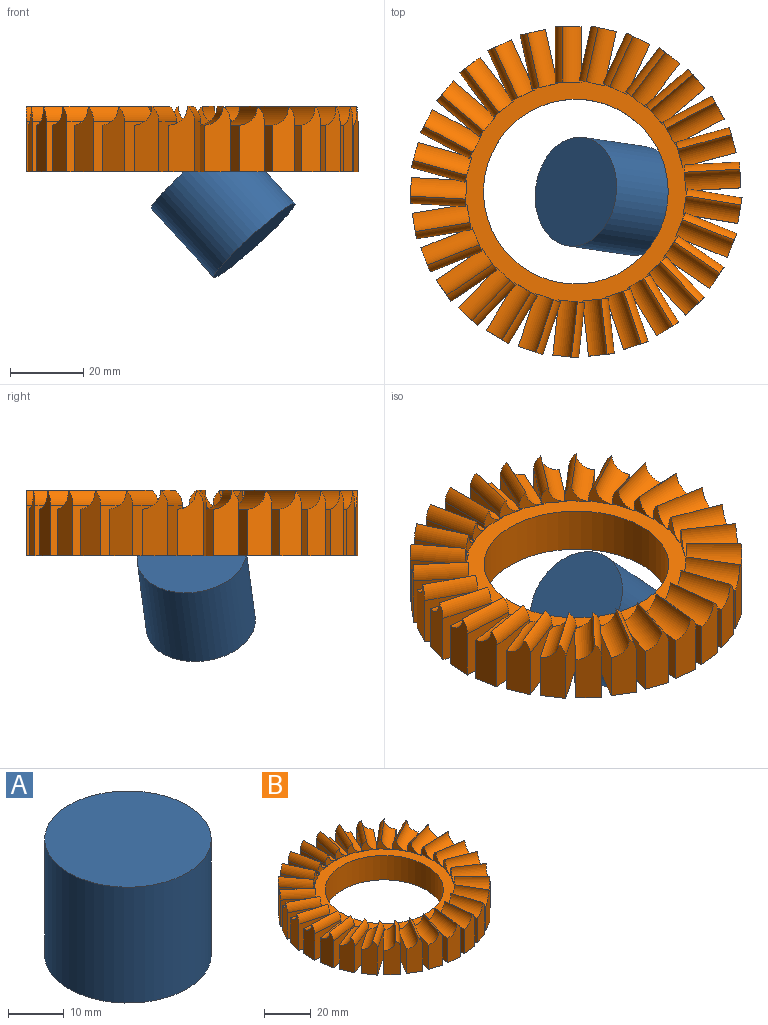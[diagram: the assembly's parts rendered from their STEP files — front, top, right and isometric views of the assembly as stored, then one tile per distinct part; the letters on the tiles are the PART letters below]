
ASSEMBLY  parts=2 mates=1
PART A: 3 faces, bbox 29.8x29.8x25.4 mm
  f0: cylinder r=14.92mm len=29.84mm, axis (0,0,1), area 2380.8mm2, adj f1,f2
  f1: plane 29.84x29.84mm, normal (0,0,-1), area 699.2mm2, adj f0
  f2: plane 29.84x29.84mm, normal (0,0,1), area 699.2mm2, adj f0
PART B: 177 faces, bbox 90.4x90.3x17.8 mm
  f0: plane 90.36x90.31mm, normal (0,0,-1), area 3892.2mm2, adj f2,f5,f8,f11,f14,f17,f20,f23
  f1: cylinder r=5.08mm len=15.82mm, axis (0.42,0.91,0), area 119.7mm2, adj f2,f3,f87,f88,f91,f92,f161
  f2: plane 13.77x12.01mm, normal (-0.8,0.61,0), area 178.2mm2, adj f0,f1,f3,f93,f94,f161
  f3: plane 5.61x5.08mm, normal (-0.61,-0.8,0), area 13.1mm2, adj f1,f2,f4,f88,f93
  f4: cylinder r=5.08mm len=15.08mm, axis (0.61,0.8,0), area 119.7mm2, adj f3,f5,f6,f88,f93,f94,f174
  f5: plane 13.77x11.5mm, normal (-0.65,0.76,0), area 178.2mm2, adj f0,f4,f6,f95,f96,f174
  f6: plane 5.37x5.08mm, normal (-0.76,-0.65,0), area 13.1mm2, adj f4,f5,f7,f88,f95
  f7: cylinder r=5.08mm len=14.78mm, axis (0.76,0.65,0), area 119.7mm2, adj f6,f8,f9,f88,f95,f96,f148
  f8: plane 13.77x13.33mm, normal (-0.47,0.88,0), area 178.2mm2, adj f0,f7,f9,f97,f98,f148
  f9: plane 6.22x5.08mm, normal (-0.88,-0.47,0), area 13.1mm2, adj f7,f8,f10,f88,f97
  f10: cylinder r=5.08mm len=15.7mm, axis (0.88,0.47,0), area 119.7mm2, adj f9,f11,f12,f88,f97,f98,f173
  f11: plane 14.53x13.77mm, normal (-0.27,0.96,0), area 178.2mm2, adj f0,f10,f12,f99,f100,f173
  f12: plane 6.78x5.08mm, normal (-0.96,-0.27,0), area 13.1mm2, adj f10,f11,f13,f88,f99
  f13: cylinder r=5.08mm len=15.89mm, axis (0.96,0.27,0), area 119.7mm2, adj f12,f14,f15,f88,f99,f100,f160
  f14: plane 15.06x13.77mm, normal (-0.05,1,0), area 178.2mm2, adj f0,f13,f15,f101,f102,f160
  f15: plane 7.03x5.08mm, normal (-1,-0.05,0), area 13.1mm2, adj f13,f14,f16,f88,f101
  f16: cylinder r=5.08mm len=15.33mm, axis (1,0.05,0), area 119.7mm2, adj f15,f17,f18,f88,f101,f102,f172
  f17: plane 14.88x13.77mm, normal (0.16,0.99,0), area 178.2mm2, adj f0,f16,f18,f103,f104,f172
  f18: plane 6.95x5.08mm, normal (-0.99,0.16,0), area 13.1mm2, adj f16,f17,f19,f88,f103
  f19: cylinder r=5.08mm len=15.7mm, axis (0.99,-0.16,0), area 119.7mm2, adj f18,f20,f21,f88,f103,f104,f149
  f20: plane 14.01x13.77mm, normal (0.37,0.93,0), area 178.2mm2, adj f0,f19,f21,f105,f106,f149
  f21: plane 6.54x5.08mm, normal (-0.93,0.37,0), area 13.1mm2, adj f19,f20,f22,f88,f105
  f22: cylinder r=5.08mm len=15.89mm, axis (0.93,-0.37,0), area 119.7mm2, adj f21,f23,f24,f88,f105,f106,f171
  f23: plane 13.77x12.48mm, normal (0.56,0.83,0), area 178.2mm2, adj f0,f22,f24,f107,f108,f171
  f24: plane 5.83x5.08mm, normal (-0.83,0.56,0), area 13.1mm2, adj f22,f23,f25,f88,f107
  f25: cylinder r=5.08mm len=15.33mm, axis (0.83,-0.56,0), area 119.7mm2, adj f24,f26,f27,f88,f107,f108,f159
  f26: plane 13.77x10.95mm, normal (0.73,0.69,0), area 178.2mm2, adj f0,f25,f27,f109,f110,f159
  f27: plane 5.11x5.08mm, normal (-0.69,0.73,0), area 13.1mm2, adj f25,f26,f28,f88,f109
  f28: cylinder r=5.08mm len=14.44mm, axis (0.69,-0.73,0), area 119.7mm2, adj f27,f29,f30,f88,f109,f110,f170
  f29: plane 13.77x12.92mm, normal (0.86,0.52,0), area 178.2mm2, adj f0,f28,f30,f111,f112,f170
  f30: plane 6.03x5.08mm, normal (-0.52,0.86,0), area 13.1mm2, adj f28,f29,f31,f88,f111
  f31: cylinder r=5.08mm len=15.54mm, axis (0.52,-0.86,0), area 119.7mm2, adj f30,f32,f33,f88,f111,f112,f158
  f32: plane 14.29x13.77mm, normal (0.95,0.32,0), area 178.2mm2, adj f0,f31,f33,f113,f114,f158
  f33: plane 6.67x5.08mm, normal (-0.32,0.95,0), area 13.1mm2, adj f31,f32,f34,f88,f113
  f34: cylinder r=5.08mm len=15.91mm, axis (0.32,-0.95,0), area 119.7mm2, adj f33,f35,f36,f88,f113,f114,f169
  f35: plane 14.99x13.77mm, normal (0.99,0.11,0), area 178.2mm2, adj f0,f34,f36,f115,f116,f169
  f36: plane 7x5.08mm, normal (-0.11,0.99,0), area 13.1mm2, adj f34,f35,f37,f88,f115
  f37: cylinder r=5.08mm len=15.54mm, axis (0.11,-0.99,0), area 119.7mm2, adj f36,f38,f39,f88,f115,f116,f157
  f38: plane 14.99x13.77mm, normal (0.99,-0.11,0), area 178.2mm2, adj f0,f37,f39,f117,f118,f157
  f39: plane 7x5.08mm, normal (0.11,0.99,0), area 13.1mm2, adj f37,f38,f40,f88,f117
  f40: cylinder r=5.08mm len=15.54mm, axis (-0.11,-0.99,0), area 119.7mm2, adj f39,f41,f42,f88,f117,f118,f168
  f41: plane 14.29x13.77mm, normal (0.95,-0.32,0), area 178.2mm2, adj f0,f40,f42,f119,f120,f168
  f42: plane 6.67x5.08mm, normal (0.32,0.95,0), area 13.1mm2, adj f40,f41,f43,f88,f119
  f43: cylinder r=5.08mm len=15.91mm, axis (-0.32,-0.95,0), area 119.7mm2, adj f42,f44,f45,f88,f119,f120,f150
  f44: plane 13.77x12.92mm, normal (0.86,-0.52,0), area 178.2mm2, adj f0,f43,f45,f121,f122,f150
  f45: plane 6.03x5.08mm, normal (0.52,0.86,0), area 13.1mm2, adj f43,f44,f46,f88,f121
  f46: cylinder r=5.08mm len=15.54mm, axis (-0.52,-0.86,0), area 119.7mm2, adj f45,f47,f48,f88,f121,f122,f167
  f47: plane 13.77x10.95mm, normal (0.73,-0.69,0), area 178.2mm2, adj f0,f46,f48,f123,f124,f167
  f48: plane 5.11x5.08mm, normal (0.69,0.73,0), area 13.1mm2, adj f46,f47,f49,f88,f123
  f49: cylinder r=5.08mm len=14.44mm, axis (-0.69,-0.73,0), area 119.7mm2, adj f48,f50,f51,f88,f123,f124,f151
  f50: plane 13.77x12.48mm, normal (0.56,-0.83,0), area 178.2mm2, adj f0,f49,f51,f125,f126,f151
  f51: plane 5.83x5.08mm, normal (0.83,0.56,0), area 13.1mm2, adj f49,f50,f52,f88,f125
  f52: cylinder r=5.08mm len=15.33mm, axis (-0.83,-0.56,0), area 119.7mm2, adj f51,f53,f54,f88,f125,f126,f166
  f53: plane 14.01x13.77mm, normal (0.37,-0.93,0), area 178.2mm2, adj f0,f52,f54,f127,f128,f166
  f54: plane 6.54x5.08mm, normal (0.93,0.37,0), area 13.1mm2, adj f52,f53,f55,f88,f127
  f55: cylinder r=5.08mm len=15.89mm, axis (-0.93,-0.37,0), area 119.7mm2, adj f54,f56,f57,f88,f127,f128,f152
  f56: plane 14.88x13.77mm, normal (0.16,-0.99,0), area 178.2mm2, adj f0,f55,f57,f129,f130,f152
  f57: plane 6.95x5.08mm, normal (0.99,0.16,0), area 13.1mm2, adj f55,f56,f58,f88,f129
  f58: cylinder r=5.08mm len=15.7mm, axis (-0.99,-0.16,0), area 119.7mm2, adj f57,f59,f60,f88,f129,f130,f165
  f59: plane 15.06x13.77mm, normal (-0.05,-1,0), area 178.2mm2, adj f0,f58,f60,f131,f132,f165
  f60: plane 7.03x5.08mm, normal (1,-0.05,0), area 13.1mm2, adj f58,f59,f61,f88,f131
  f61: cylinder r=5.08mm len=15.33mm, axis (-1,0.05,0), area 119.7mm2, adj f60,f62,f63,f88,f131,f132,f153
  f62: plane 14.53x13.77mm, normal (-0.27,-0.96,0), area 178.2mm2, adj f0,f61,f63,f133,f134,f153
  f63: plane 6.78x5.08mm, normal (0.96,-0.27,0), area 13.1mm2, adj f61,f62,f64,f88,f133
  f64: cylinder r=5.08mm len=15.89mm, axis (-0.96,0.27,0), area 119.7mm2, adj f63,f65,f66,f88,f133,f134,f164
  f65: plane 13.77x13.33mm, normal (-0.47,-0.88,0), area 178.2mm2, adj f0,f64,f66,f135,f136,f164
  f66: plane 6.22x5.08mm, normal (0.88,-0.47,0), area 13.1mm2, adj f64,f65,f67,f88,f135
  f67: cylinder r=5.08mm len=15.7mm, axis (-0.88,0.47,0), area 119.7mm2, adj f66,f68,f69,f88,f135,f136,f154
  f68: plane 13.77x11.5mm, normal (-0.65,-0.76,0), area 178.2mm2, adj f0,f67,f69,f137,f138,f154
  f69: plane 5.37x5.08mm, normal (0.76,-0.65,0), area 13.1mm2, adj f67,f68,f70,f88,f137
  f70: cylinder r=5.08mm len=14.78mm, axis (-0.76,0.65,0), area 119.7mm2, adj f69,f71,f72,f88,f137,f138,f163
  f71: plane 13.77x12.01mm, normal (-0.8,-0.61,0), area 178.2mm2, adj f0,f70,f72,f139,f140,f163
  f72: plane 5.61x5.08mm, normal (0.61,-0.8,0), area 13.1mm2, adj f70,f71,f73,f88,f139
  f73: cylinder r=5.08mm len=15.08mm, axis (-0.61,0.8,0), area 119.7mm2, adj f72,f74,f75,f88,f139,f140,f155
  f74: plane 13.77x13.69mm, normal (-0.91,-0.42,0), area 178.2mm2, adj f0,f73,f75,f141,f142,f155
  f75: plane 6.39x5.08mm, normal (0.42,-0.91,0), area 13.1mm2, adj f73,f74,f76,f88,f141
  f76: cylinder r=5.08mm len=15.82mm, axis (-0.42,0.91,0), area 119.7mm2, adj f75,f77,f78,f88,f141,f142,f162
  f77: plane 14.73x13.77mm, normal (-0.98,-0.21,0), area 178.2mm2, adj f0,f76,f78,f143,f144,f162
  f78: plane 6.88x5.08mm, normal (0.21,-0.98,0), area 13.1mm2, adj f76,f77,f79,f88,f143
  f79: cylinder r=5.08mm len=15.82mm, axis (-0.21,0.98,0), area 119.7mm2, adj f78,f80,f81,f88,f143,f144,f156
  f80: plane 15.08x13.77mm, normal (-1,0,0), area 178.2mm2, adj f0,f79,f81,f146,f147,f156
  f81: plane 7.04x5.08mm, normal (0,-1,0), area 13.1mm2, adj f79,f80,f82,f88,f147
  f82: cylinder r=5.08mm len=15.08mm, axis (0,1,0), area 119.7mm2, adj f81,f83,f84,f88,f146,f147,f176
  f83: plane 14.73x13.77mm, normal (-0.98,0.21,0), area 178.2mm2, adj f0,f82,f84,f89,f90,f176
  f84: plane 6.88x5.08mm, normal (-0.21,-0.98,0), area 13.1mm2, adj f82,f83,f85,f88,f89
  f85: cylinder r=5.08mm len=15.82mm, axis (0.21,0.98,0), area 119.7mm2, adj f84,f86,f87,f88,f89,f90,f175
  f86: plane 13.77x13.69mm, normal (-0.91,0.42,0), area 178.2mm2, adj f0,f85,f87,f91,f92,f175
  f87: plane 6.39x5.08mm, normal (-0.42,-0.91,0), area 13.1mm2, adj f1,f85,f86,f88,f91
  f88: plane 60.43x60.36mm, normal (0,0,1), area 830.3mm2, adj f1,f3,f4,f6,f7,f9,f10,f12
  f89: cylinder r=5.08mm len=15.15mm, axis (0.21,0.98,0), area 69.7mm2, adj f83,f84,f85,f90
  f90: plane 17.78x6.88mm, normal (0.21,0.98,0), area 102.5mm2, adj f0,f83,f85,f89,f175
  f91: cylinder r=5.08mm len=14.51mm, axis (0.42,0.91,0), area 69.7mm2, adj f1,f86,f87,f92
  f92: plane 17.78x6.39mm, normal (0.42,0.91,0), area 102.5mm2, adj f0,f1,f86,f91,f161
  f93: cylinder r=5.08mm len=13.19mm, axis (0.61,0.8,0), area 69.7mm2, adj f2,f3,f4,f94
  f94: plane 17.78x5.61mm, normal (0.61,0.8,0), area 102.5mm2, adj f0,f2,f4,f93,f174
  f95: cylinder r=5.08mm len=12.76mm, axis (0.76,0.65,0), area 69.7mm2, adj f5,f6,f7,f96
  f96: plane 17.78x5.37mm, normal (0.76,0.65,0), area 102.5mm2, adj f0,f5,f7,f95,f148
  f97: cylinder r=5.08mm len=14.24mm, axis (0.88,0.47,0), area 69.7mm2, adj f8,f9,f10,f98
  f98: plane 17.78x6.22mm, normal (0.88,0.47,0), area 102.5mm2, adj f0,f8,f10,f97,f173
  f99: cylinder r=5.08mm len=15.05mm, axis (0.96,0.27,0), area 69.7mm2, adj f11,f12,f13,f100
  f100: plane 17.78x6.78mm, normal (0.96,0.27,0), area 102.5mm2, adj f0,f11,f13,f99,f160
  f101: cylinder r=5.08mm len=15.16mm, axis (1,0.05,0), area 69.7mm2, adj f14,f15,f16,f102
  f102: plane 17.78x7.03mm, normal (1,0.05,0), area 102.5mm2, adj f0,f14,f16,f101,f172
  f103: cylinder r=5.08mm len=15.2mm, axis (0.99,-0.16,0), area 69.7mm2, adj f17,f18,f19,f104
  f104: plane 17.78x6.95mm, normal (0.99,-0.16,0), area 102.5mm2, adj f0,f17,f19,f103,f149
  f105: cylinder r=5.08mm len=14.73mm, axis (0.93,-0.37,0), area 69.7mm2, adj f20,f21,f22,f106
  f106: plane 17.78x6.54mm, normal (0.93,-0.37,0), area 102.5mm2, adj f0,f20,f22,f105,f171
  f107: cylinder r=5.08mm len=13.58mm, axis (0.83,-0.56,0), area 69.7mm2, adj f23,f24,f25,f108
  f108: plane 17.78x5.83mm, normal (0.83,-0.56,0), area 102.5mm2, adj f0,f23,f25,f107,f159
  f109: cylinder r=5.08mm len=12.3mm, axis (0.69,-0.73,0), area 69.7mm2, adj f26,f27,f28,f110
  f110: plane 17.78x5.11mm, normal (0.69,-0.73,0), area 102.5mm2, adj f0,f26,f28,f109,f170
  f111: cylinder r=5.08mm len=13.93mm, axis (0.52,-0.86,0), area 69.7mm2, adj f29,f30,f31,f112
  f112: plane 17.78x6.03mm, normal (0.52,-0.86,0), area 102.5mm2, adj f0,f29,f31,f111,f158
  f113: cylinder r=5.08mm len=14.92mm, axis (0.32,-0.95,0), area 69.7mm2, adj f32,f33,f34,f114
  f114: plane 17.78x6.67mm, normal (0.32,-0.95,0), area 102.5mm2, adj f0,f32,f34,f113,f169
  f115: cylinder r=5.08mm len=15.2mm, axis (0.11,-0.99,0), area 69.7mm2, adj f35,f36,f37,f116
  f116: plane 17.78x7mm, normal (0.11,-0.99,0), area 102.5mm2, adj f0,f35,f37,f115,f157
  f117: cylinder r=5.08mm len=15.2mm, axis (-0.11,-0.99,0), area 69.7mm2, adj f38,f39,f40,f118
  f118: plane 17.78x7mm, normal (-0.11,-0.99,0), area 102.5mm2, adj f0,f38,f40,f117,f168
  f119: cylinder r=5.08mm len=14.92mm, axis (-0.32,-0.95,0), area 69.7mm2, adj f41,f42,f43,f120
  f120: plane 17.78x6.67mm, normal (-0.32,-0.95,0), area 102.5mm2, adj f0,f41,f43,f119,f150
  f121: cylinder r=5.08mm len=13.93mm, axis (-0.52,-0.86,0), area 69.7mm2, adj f44,f45,f46,f122
  f122: plane 17.78x6.03mm, normal (-0.52,-0.86,0), area 102.5mm2, adj f0,f44,f46,f121,f167
  f123: cylinder r=5.08mm len=12.3mm, axis (-0.69,-0.73,0), area 69.7mm2, adj f47,f48,f49,f124
  f124: plane 17.78x5.11mm, normal (-0.69,-0.73,0), area 102.5mm2, adj f0,f47,f49,f123,f151
  f125: cylinder r=5.08mm len=13.58mm, axis (-0.83,-0.56,0), area 69.7mm2, adj f50,f51,f52,f126
  f126: plane 17.78x5.83mm, normal (-0.83,-0.56,0), area 102.5mm2, adj f0,f50,f52,f125,f166
  f127: cylinder r=5.08mm len=14.73mm, axis (-0.93,-0.37,0), area 69.7mm2, adj f53,f54,f55,f128
  f128: plane 17.78x6.54mm, normal (-0.93,-0.37,0), area 102.5mm2, adj f0,f53,f55,f127,f152
  f129: cylinder r=5.08mm len=15.2mm, axis (-0.99,-0.16,0), area 69.7mm2, adj f56,f57,f58,f130
  f130: plane 17.78x6.95mm, normal (-0.99,-0.16,0), area 102.5mm2, adj f0,f56,f58,f129,f165
  f131: cylinder r=5.08mm len=15.16mm, axis (-1,0.05,0), area 69.7mm2, adj f59,f60,f61,f132
  f132: plane 17.78x7.03mm, normal (-1,0.05,0), area 102.5mm2, adj f0,f59,f61,f131,f153
  f133: cylinder r=5.08mm len=15.05mm, axis (-0.96,0.27,0), area 69.7mm2, adj f62,f63,f64,f134
  f134: plane 17.78x6.78mm, normal (-0.96,0.27,0), area 102.5mm2, adj f0,f62,f64,f133,f164
  f135: cylinder r=5.08mm len=14.24mm, axis (-0.88,0.47,0), area 69.7mm2, adj f65,f66,f67,f136
  f136: plane 17.78x6.22mm, normal (-0.88,0.47,0), area 102.5mm2, adj f0,f65,f67,f135,f154
  f137: cylinder r=5.08mm len=12.76mm, axis (-0.76,0.65,0), area 69.7mm2, adj f68,f69,f70,f138
  f138: plane 17.78x5.37mm, normal (-0.76,0.65,0), area 102.5mm2, adj f0,f68,f70,f137,f163
  f139: cylinder r=5.08mm len=13.19mm, axis (-0.61,0.8,0), area 69.7mm2, adj f71,f72,f73,f140
  f140: plane 17.78x5.61mm, normal (-0.61,0.8,0), area 102.5mm2, adj f0,f71,f73,f139,f155
  f141: cylinder r=5.08mm len=14.51mm, axis (-0.42,0.91,0), area 69.7mm2, adj f74,f75,f76,f142
  f142: plane 17.78x6.39mm, normal (-0.42,0.91,0), area 102.5mm2, adj f0,f74,f76,f141,f162
  f143: cylinder r=5.08mm len=15.15mm, axis (-0.21,0.98,0), area 69.7mm2, adj f77,f78,f79,f144
  f144: plane 17.78x6.88mm, normal (-0.21,0.98,0), area 102.5mm2, adj f0,f77,f79,f143,f156
  f145: cylinder r=25.14mm len=50.28mm, axis (0,0,-1), area 2006mm2, adj f0,f88
  f146: plane 17.78x7.04mm, normal (0,1,0), area 102.5mm2, adj f0,f80,f82,f147,f176
  f147: cylinder r=5.08mm len=15.08mm, axis (0,1,0), area 69.7mm2, adj f80,f81,f82,f146
  f148: plane 12.7x9.37mm, normal (0.65,-0.76,0), area 156.2mm2, adj f0,f7,f8,f96
  f149: plane 12.7x12.14mm, normal (-0.16,-0.99,0), area 156.2mm2, adj f0,f19,f20,f104
  f150: plane 12.7x11.66mm, normal (-0.95,0.32,0), area 156.2mm2, adj f0,f43,f44,f120
  f151: plane 12.7x8.93mm, normal (-0.73,0.69,0), area 156.2mm2, adj f0,f49,f50,f124
  f152: plane 12.7x11.43mm, normal (-0.37,0.93,0), area 156.2mm2, adj f0,f55,f56,f128
  f153: plane 12.7x12.28mm, normal (0.05,1,0), area 156.2mm2, adj f0,f61,f62,f132
  f154: plane 12.7x10.87mm, normal (0.47,0.88,0), area 156.2mm2, adj f0,f67,f68,f136
  f155: plane 12.7x9.79mm, normal (0.8,0.61,0), area 156.2mm2, adj f0,f73,f74,f140
  f156: plane 12.7x12.01mm, normal (0.98,0.21,0), area 156.2mm2, adj f0,f79,f80,f144
  f157: plane 12.7x12.23mm, normal (-0.99,-0.11,0), area 156.2mm2, adj f0,f37,f38,f116
  f158: plane 12.7x10.54mm, normal (-0.86,-0.52,0), area 156.2mm2, adj f0,f31,f32,f112
  f159: plane 12.7x10.18mm, normal (-0.56,-0.83,0), area 156.2mm2, adj f0,f25,f26,f108
  f160: plane 12.7x11.85mm, normal (0.27,-0.96,0), area 156.2mm2, adj f0,f13,f14,f100
  f161: plane 12.7x11.16mm, normal (0.91,-0.42,0), area 156.2mm2, adj f0,f1,f2,f92
  f162: plane 12.7x11.16mm, normal (0.91,0.42,0), area 156.2mm2, adj f0,f76,f77,f142
  f163: plane 12.7x9.37mm, normal (0.65,0.76,0), area 156.2mm2, adj f0,f70,f71,f138
  f164: plane 12.7x11.85mm, normal (0.27,0.96,0), area 156.2mm2, adj f0,f64,f65,f134
  f165: plane 12.7x12.14mm, normal (-0.16,0.99,0), area 156.2mm2, adj f0,f58,f59,f130
  f166: plane 12.7x10.18mm, normal (-0.56,0.83,0), area 156.2mm2, adj f0,f52,f53,f126
  f167: plane 12.7x10.54mm, normal (-0.86,0.52,0), area 156.2mm2, adj f0,f46,f47,f122
  f168: plane 12.7x12.23mm, normal (-0.99,0.11,0), area 156.2mm2, adj f0,f40,f41,f118
  f169: plane 12.7x11.66mm, normal (-0.95,-0.32,0), area 156.2mm2, adj f0,f34,f35,f114
  f170: plane 12.7x8.93mm, normal (-0.73,-0.69,0), area 156.2mm2, adj f0,f28,f29,f110
  f171: plane 12.7x11.43mm, normal (-0.37,-0.93,0), area 156.2mm2, adj f0,f22,f23,f106
  f172: plane 12.7x12.28mm, normal (0.05,-1,0), area 156.2mm2, adj f0,f16,f17,f102
  f173: plane 12.7x10.87mm, normal (0.47,-0.88,0), area 156.2mm2, adj f0,f10,f11,f98
  f174: plane 12.7x9.79mm, normal (0.8,-0.61,0), area 156.2mm2, adj f0,f4,f5,f94
  f175: plane 12.7x12.01mm, normal (0.98,-0.21,0), area 156.2mm2, adj f0,f85,f86,f90
  f176: plane 12.7x12.3mm, normal (1,0,0), area 156.2mm2, adj f0,f82,f83,f146
PLACE A rot(axis=(0.9,0.29,0.33),161.6deg) t=(32.94,48.27,-38.88)mm
PLACE B t=(11.24,22.61,-20.7)mm fixed
MATE ball A.f0 <-> B.f145  axis (-0.67,0.1,0.74) through (11.24,22.61,-20.7)mm
